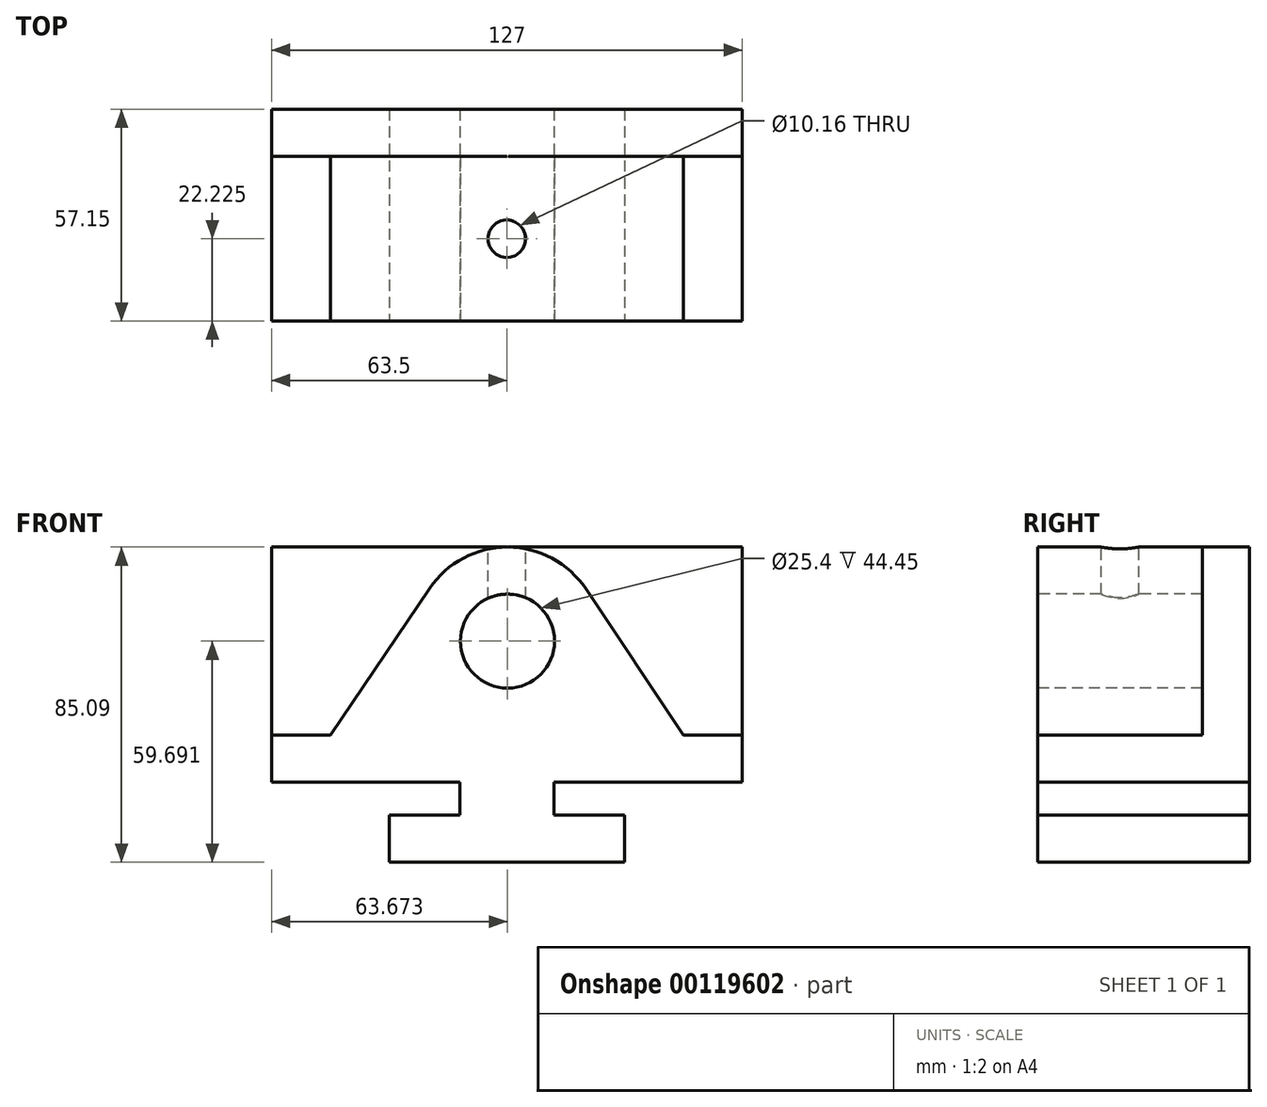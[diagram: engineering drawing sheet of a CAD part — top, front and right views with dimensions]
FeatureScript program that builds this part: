
annotation { "Feature Type Name" : "Feature", "Feature Type Description" : "" }
export const myFeature = defineFeature(function(context is Context, id is Id, definition is map)
    precondition{}
    {
        {
            var Q0;
            Q0=qCreatedBy(makeId("Front.planeOp"),FACE);
            var sketch = newSketch(context, id + "F0", { "sketchPlane" : qUnion([Q0])});
            skLineSegment(sketch, "E0.bottom", {"start": v(0, 0) * mm, "end": v(127, 0) * mm});
            skLineSegment(sketch, "E0.top", {"start": v(0, 63.5) * mm, "end": v(127, 63.5) * mm});
            skLineSegment(sketch, "E0.left", {"start": v(0, 0) * mm, "end": v(0, 63.5) * mm});
            skLineSegment(sketch, "E0.right", {"start": v(127, 0) * mm, "end": v(127, 63.5) * mm});
            skSolve(sketch);
        }
        {
            var Q0;
            Q0 = qSketchRegion(id + "F0", true);
            extrude(context, id + "F1", {"entities" : qUnion([Q0]), "depth" : 12.7 * mm});
        }
        {
            var Q0;
            Q0=makeQuery(id+"F1.opExtrude","CAP_FACE",FACE,{"disambiguationData":[OSD([sQuery(id+"F0.wireOp",EDGE,"E0.bottom"),sQuery(id+"F0.wireOp",EDGE,"E0.top"),sQuery(id+"F0.wireOp",EDGE,"E0.left"),sQuery(id+"F0.wireOp",EDGE,"E0.right")])],"isStart":false});
            var sketch = newSketch(context, id + "F2", { "sketchPlane" : qUnion([Q0])});
            skLineSegment(sketch, "E1", {"start": v(0, 0) * mm, "end": v(127, 0) * mm});
            skLineSegment(sketch, "E2", {"start": v(127, 0) * mm, "end": v(127, 12.7) * mm});
            skLineSegment(sketch, "E3", {"start": v(127, 12.7) * mm, "end": v(111.13, 12.7) * mm});
            skLineSegment(sketch, "E4", {"start": v(0, 0) * mm, "end": v(0, 12.7) * mm});
            skLineSegment(sketch, "E5", {"start": v(0, 12.7) * mm, "end": v(15.88, 12.7) * mm});
            skLineSegment(sketch, "E6", {"start": v(63.5, 63.5) * mm, "end": v(63.5, 0) * mm, "construction": true});
            skLineSegment(sketch, "E7", {"start": v(15.87, 12.7) * mm, "end": v(42.62, 52.31) * mm});
            skLineSegment(sketch, "E8", {"start": v(111.13, 12.7) * mm, "end": v(84.8, 52.19) * mm});
            skArc(sketch, "E9", {"start": v(84.8, 52.19) * mm, "mid": v(63.75, 63.5) * mm, "end": v(42.62, 52.31) * mm});
            skSolve(sketch);
        }
        {
            var Q0;
            Q0 = qSketchRegion(id + "F2", true);
            extrude(context, id + "F3", {"entities" : qUnion([Q0]), "operationType" : NewBodyOperationType.ADD, "depth" : 44.45 * mm});
        }
        {
            var Q0;
            Q0=makeQuery(id+"F3.opExtrude","CAP_FACE",FACE,{"disambiguationData":[OSD([sQuery(id+"F2.wireOp",EDGE,"E1"),sQuery(id+"F2.wireOp",EDGE,"E2"),sQuery(id+"F2.wireOp",EDGE,"E3"),sQuery(id+"F2.wireOp",EDGE,"E4"),sQuery(id+"F2.wireOp",EDGE,"E5"),sQuery(id+"F2.wireOp",EDGE,"E7"),sQuery(id+"F2.wireOp",EDGE,"E8"),sQuery(id+"F2.wireOp",EDGE,"E9")])],"isStart":false});
            var sketch = newSketch(context, id + "F4", { "sketchPlane" : qUnion([Q0])});
            skLineSegment(sketch, "E10", {"start": v(0, 0) * mm, "end": v(63.5, 0) * mm, "construction": true});
            skLineSegment(sketch, "E11", {"start": v(63.5, 0) * mm, "end": v(63.5, 63.5) * mm, "construction": true});
            skCircle(sketch, "E12", {"center": v(63.67, 38.1) * mm, "radius": 12.7 * mm});
            skSolve(sketch);
        }
        {
            var Q0;
            Q0 = qSketchRegion(id + "F4", true);
            extrude(context, id + "F5", {"entities" : qUnion([Q0]), "operationType" : NewBodyOperationType.REMOVE, "oppositeDirection" : true, "depth" : 44.45 * mm});
        }
        {
            var Q0;
            Q0=makeQuery(id+"F3.opExtrude","CAP_FACE",FACE,{"disambiguationData":[OSD([sQuery(id+"F2.wireOp",EDGE,"E1"),sQuery(id+"F2.wireOp",EDGE,"E2"),sQuery(id+"F2.wireOp",EDGE,"E3"),sQuery(id+"F2.wireOp",EDGE,"E4"),sQuery(id+"F2.wireOp",EDGE,"E5"),sQuery(id+"F2.wireOp",EDGE,"E7"),sQuery(id+"F2.wireOp",EDGE,"E8"),sQuery(id+"F2.wireOp",EDGE,"E9")])],"isStart":false});
            var sketch = newSketch(context, id + "F6", { "sketchPlane" : qUnion([Q0])});
            skLineSegment(sketch, "E13", {"start": v(50.8, 0) * mm, "end": v(50.8, -8.9) * mm});
            skLineSegment(sketch, "E14", {"start": v(50.8, -8.9) * mm, "end": v(31.75, -8.9) * mm});
            skLineSegment(sketch, "E15", {"start": v(31.75, -8.9) * mm, "end": v(31.75, -21.59) * mm});
            skLineSegment(sketch, "E16", {"start": v(31.75, -21.6) * mm, "end": v(95.25, -21.6) * mm});
            skLineSegment(sketch, "E17", {"start": v(95.25, -21.59) * mm, "end": v(95.25, -8.9) * mm});
            skLineSegment(sketch, "E18", {"start": v(95.25, -8.9) * mm, "end": v(76.2, -8.9) * mm});
            skLineSegment(sketch, "E19", {"start": v(76.2, -8.9) * mm, "end": v(76.2, 0) * mm});
            skLineSegment(sketch, "E20", {"start": v(50.8, 0) * mm, "end": v(76.2, 0) * mm});
            skSolve(sketch);
        }
        {
            var Q0;
            Q0 = qSketchRegion(id + "F6", true);
            extrude(context, id + "F7", {"entities" : qUnion([Q0]), "operationType" : NewBodyOperationType.ADD, "oppositeDirection" : true, "depth" : 57.15 * mm});
        }
        {
            var Q0;
            Q0=makeQuery(id+"F1.opExtrude","SWEPT_FACE",FACE,{"disambiguationData":[OSD([sQuery(id+"F0.wireOp",EDGE,"E0.top")])]});
            var sketch = newSketch(context, id + "F8", { "sketchPlane" : qUnion([Q0])});
            skLineSegment(sketch, "E21", {"start": v(63.5, 0) * mm, "end": v(63.5, -34.93) * mm, "construction": true});
            skCircle(sketch, "E22", {"center": v(63.5, -34.93) * mm, "radius": 5.08 * mm});
            skSolve(sketch);
        }
        {
            var Q0;
            Q0 = qSketchRegion(id + "F8", true);
            var Q1;
            Q1=makeQuery(id+"F5.boolean.opBoolean","COPY",FACE,{"derivedFrom":makeQuery(id+"F5.opExtrude","SWEPT_FACE",FACE,{"disambiguationData":[OSD([sQuery(id+"F4.wireOp",EDGE,"E12")])]})});
            extrude(context, id + "F9", {"entities" : qUnion([Q0]), "operationType" : NewBodyOperationType.REMOVE, "endBound" : BoundingType.UP_TO_SURFACE, "oppositeDirection" : true, "endBoundEntityFace" : qUnion([Q1]), "depth" : 25.4 * mm, "hasSecondDirection" : true, "secondDirectionBound" : SecondDirectionBoundingType.THROUGH_ALL, "secondDirectionOppositeDirection" : false, "secondDirectionDepth" : 25.4 * mm});
        }
    });
